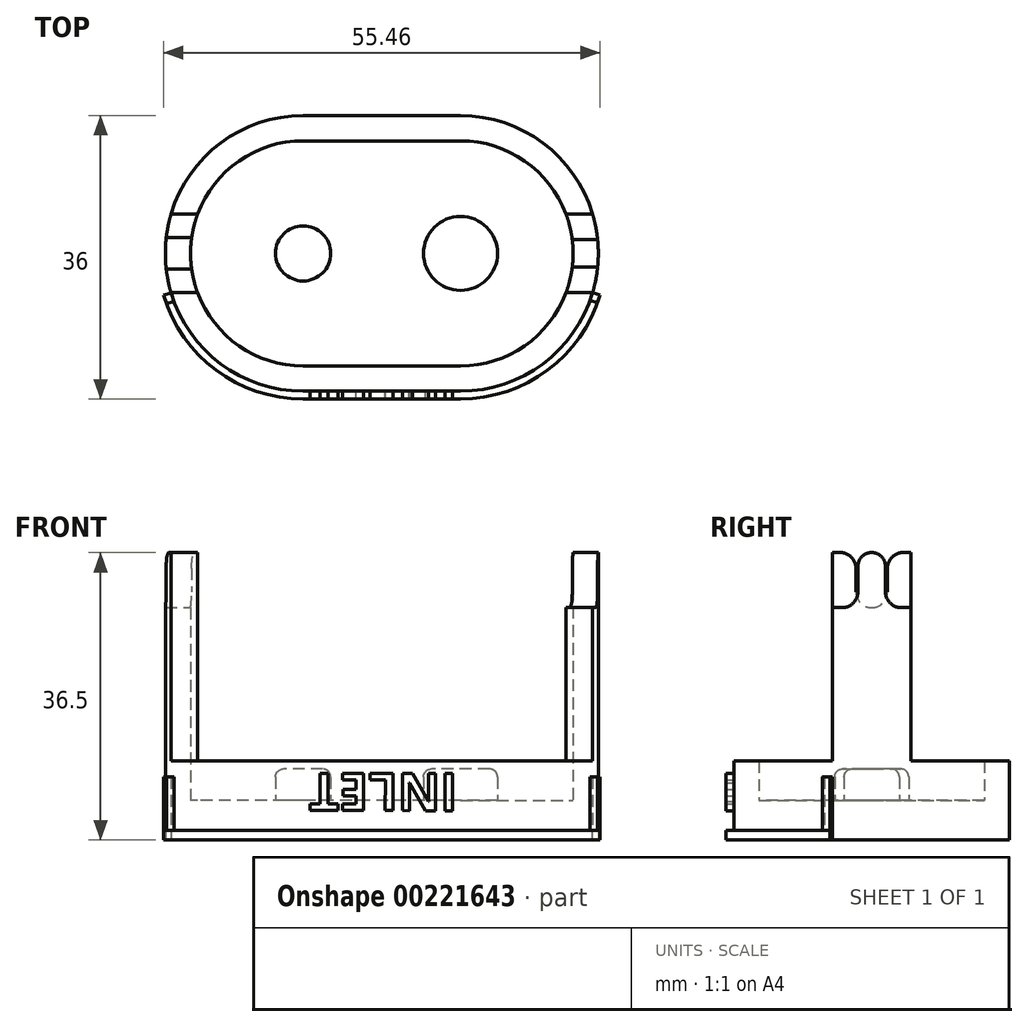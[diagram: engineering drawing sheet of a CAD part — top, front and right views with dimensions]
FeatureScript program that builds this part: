
annotation { "Feature Type Name" : "Feature", "Feature Type Description" : "" }
export const myFeature = defineFeature(function(context is Context, id is Id, definition is map)
    precondition{}
    {
        {
            var Q0;
            Q0=qCreatedBy(makeId("Top.planeOp"),FACE);
            var sketch = newSketch(context, id + "F0", { "sketchPlane" : qUnion([Q0])});
            skArc(sketch, "E0", {"start": v(0, -17.5) * mm, "mid": v(17.5, 0) * mm, "end": v(0, 17.5) * mm});
            skArc(sketch, "E1", {"start": v(-20, 17.5) * mm, "mid": v(-37.5, 0) * mm, "end": v(-20, -17.5) * mm});
            skLineSegment(sketch, "E2", {"start": v(-20, 17.5) * mm, "end": v(0, 17.5) * mm});
            skLineSegment(sketch, "E3", {"start": v(-20, -17.5) * mm, "end": v(0, -17.5) * mm});
            skSolve(sketch);
        }
        {
            var Q0;
            Q0=makeQuery(id+"F0.imprint","IMPRINT",FACE,{"disambiguationData":[TD([[makeQuery(id+"F0.imprint","IMPRINT",EDGE,{"derivedFrom":sQuery(id+"F0.wireOp",EDGE,"E0")}),1.0]])]});
            extrude(context, id + "F1", {"entities" : qUnion([Q0]), "depth" : 5 * mm});
        }
        {
            var Q0;
            Q0=qCreatedBy(makeId("Top.planeOp"),FACE);
            var sketch = newSketch(context, id + "F2", { "sketchPlane" : qUnion([Q0])});
            skArc(sketch, "E4", {"start": v(0, -17.5) * mm, "mid": v(17.5, 0) * mm, "end": v(0, 17.5) * mm});
            skArc(sketch, "E5", {"start": v(-20, 17.5) * mm, "mid": v(-37.5, 0) * mm, "end": v(-20, -17.5) * mm});
            skLineSegment(sketch, "E6", {"start": v(-20, 17.5) * mm, "end": v(0, 17.5) * mm});
            skLineSegment(sketch, "E7", {"start": v(-20, -17.5) * mm, "end": v(0, -17.5) * mm});
            skLineSegment(sketch, "E8.0", {"start": v(-20, 14.3) * mm, "end": v(0, 14.3) * mm});
            skArc(sketch, "E8.1", {"start": v(-20, 14.3) * mm, "mid": v(-34.3, 0) * mm, "end": v(-20, -14.3) * mm});
            skLineSegment(sketch, "E8.2", {"start": v(-20, -14.3) * mm, "end": v(0, -14.3) * mm});
            skArc(sketch, "E8.3", {"start": v(0, -14.3) * mm, "mid": v(14.3, 0) * mm, "end": v(0, 14.3) * mm});
            skSolve(sketch);
        }
        {
            var Q0;
            Q0 = qSketchRegion(id + "F2", true);
            extrude(context, id + "F3", {"entities" : qUnion([Q0]), "operationType" : NewBodyOperationType.ADD, "depth" : 10 * mm});
        }
        {
            var Q0;
            Q0=qCreatedBy(makeId("Top.planeOp"),FACE);
            var sketch = newSketch(context, id + "F4", { "sketchPlane" : qUnion([Q0])});
            skArc(sketch, "E9", {"start": v(16.77, -5) * mm, "mid": v(17.5, 0) * mm, "end": v(16.77, 5) * mm});
            skArc(sketch, "E10", {"start": v(-36.77, 5) * mm, "mid": v(-37.5, 0) * mm, "end": v(-36.77, -5) * mm});
            skArc(sketch, "E11.1", {"start": v(-33.4, 5) * mm, "mid": v(-34.3, 0) * mm, "end": v(-33.4, -5) * mm});
            skLineSegment(sketch, "E12.bottom", {"start": v(16.77, 5) * mm, "end": v(13.4, 5) * mm});
            skLineSegment(sketch, "E12.top", {"start": v(16.77, -5) * mm, "end": v(13.4, -5) * mm});
            skPoint(sketch, "E13.middle", {"position": v(-10, 0) * mm});
            skLineSegment(sketch, "E14.trimOffspring", {"start": v(-33.4, 5) * mm, "end": v(-36.77, 5) * mm});
            skLineSegment(sketch, "E15.trimOffspring", {"start": v(-33.4, -5) * mm, "end": v(-36.77, -5) * mm});
            skPoint(sketch, "E16", {"position": v(-34.3, 0) * mm});
            skArc(sketch, "E17", {"start": v(13.4, -5) * mm, "mid": v(14.3, 0) * mm, "end": v(13.4, 5) * mm});
            skSolve(sketch);
        }
        {
            var Q0;
            Q0=makeQuery(id+"F4.imprint","IMPRINT",FACE,{"disambiguationData":[TD([[makeQuery(id+"F4.imprint","IMPRINT",EDGE,{"derivedFrom":sQuery(id+"F4.wireOp",EDGE,"E9")}),1.0]])]});
            var Q1;
            Q1=makeQuery(id+"F4.imprint","IMPRINT",FACE,{"disambiguationData":[TD([[makeQuery(id+"F4.imprint","IMPRINT",EDGE,{"derivedFrom":sQuery(id+"F4.wireOp",EDGE,"E10")}),1.0]])]});
            extrude(context, id + "F5", {"entities" : qUnion([Q0, Q1]), "operationType" : NewBodyOperationType.ADD, "depth" : 36.5 * mm});
        }
        {
            var Q0;
            Q0=qCreatedBy(makeId("Right.planeOp"),FACE);
            var sketch = newSketch(context, id + "F6", { "sketchPlane" : qUnion([Q0])});
            skLineSegment(sketch, "E18.bottom", {"start": v(-2, 29.5) * mm, "end": v(2, 29.5) * mm});
            skLineSegment(sketch, "E18.top", {"start": v(-2, 39.5) * mm, "end": v(2, 39.5) * mm});
            skLineSegment(sketch, "E18.left", {"start": v(-2, 29.5) * mm, "end": v(-2, 39.5) * mm});
            skLineSegment(sketch, "E18.right", {"start": v(2, 29.5) * mm, "end": v(2, 39.5) * mm});
            skPoint(sketch, "E18.middle", {"position": v(0, 34.5) * mm});
            skSolve(sketch);
        }
        {
            var Q0;
            Q0=makeQuery(id+"F6.imprint","IMPRINT",FACE,{"disambiguationData":[TD([[makeQuery(id+"F6.imprint","IMPRINT",EDGE,{"derivedFrom":sQuery(id+"F6.wireOp",EDGE,"E18.bottom")}),1.0]])]});
            extrude(context, id + "F7", {"entities" : qUnion([Q0]), "operationType" : NewBodyOperationType.REMOVE, "oppositeDirection" : true, "depth" : 43.6 * mm});
        }
        {
            var Q0;
            Q0=qCreatedBy(makeId("Right.planeOp"),FACE);
            var sketch = newSketch(context, id + "F8", { "sketchPlane" : qUnion([Q0])});
            skLineSegment(sketch, "E19.bottom", {"start": v(-1.75, 29.5) * mm, "end": v(-5.7, 29.5) * mm});
            skLineSegment(sketch, "E19.top", {"start": v(-1.75, 39.5) * mm, "end": v(-5.7, 39.5) * mm});
            skLineSegment(sketch, "E19.left", {"start": v(-1.75, 29.5) * mm, "end": v(-1.75, 39.5) * mm});
            skLineSegment(sketch, "E19.right", {"start": v(-5.7, 29.5) * mm, "end": v(-5.7, 39.5) * mm});
            skPoint(sketch, "E19.middle", {"position": v(-3.72, 34.5) * mm});
            skLineSegment(sketch, "E20.bottom", {"start": v(5.7, 29.5) * mm, "end": v(1.75, 29.5) * mm});
            skLineSegment(sketch, "E20.top", {"start": v(5.7, 39.5) * mm, "end": v(1.75, 39.5) * mm});
            skLineSegment(sketch, "E20.left", {"start": v(5.7, 29.5) * mm, "end": v(5.7, 39.5) * mm});
            skLineSegment(sketch, "E20.right", {"start": v(1.75, 29.5) * mm, "end": v(1.75, 39.5) * mm});
            skPoint(sketch, "E20.middle", {"position": v(3.72, 34.5) * mm});
            skLineSegment(sketch, "E21", {"start": v(-3.72, 34.5) * mm, "end": v(3.72, 34.5) * mm});
            skPoint(sketch, "E22", {"position": v(0, 34.5) * mm});
            skSolve(sketch);
        }
        {
            var Q0;
            {var subQ1=sQuery(id+"F8.wireOp",EDGE,"E20.bottom");Q0=makeQuery(id+"F8.imprint","IMPRINT",FACE,{"disambiguationData":[TD([[makeQuery(id+"F8.imprint","IMPRINT",EDGE,{"derivedFrom":subQ1}),-1.0]])]});}
            var Q1;
            {var subQ3=sQuery(id+"F8.wireOp",EDGE,"E19.bottom");Q1=makeQuery(id+"F8.imprint","IMPRINT",FACE,{"disambiguationData":[TD([[makeQuery(id+"F8.imprint","IMPRINT",EDGE,{"derivedFrom":subQ3}),-1.0]])]});}
            extrude(context, id + "F9", {"entities" : qUnion([Q0, Q1]), "operationType" : NewBodyOperationType.REMOVE, "depth" : 25 * mm});
        }
        {
            var Q0;
            Q0=makeQuery(id+"F7.boolean.opBoolean","COPY",EDGE,{"derivedFrom":makeQuery(id+"F7.opExtrude","SWEPT_EDGE",EDGE,{"disambiguationData":[OSD([sQuery(id+"F6.wireOp",EDGE,"E18.bottom"),sQuery(id+"F6.wireOp",EDGE,"E18.left")])]})});
            var Q1;
            Q1=makeQuery(id+"F7.boolean.opBoolean","COPY",EDGE,{"derivedFrom":makeQuery(id+"F7.opExtrude","SWEPT_EDGE",EDGE,{"disambiguationData":[OSD([sQuery(id+"F6.wireOp",EDGE,"E18.bottom"),sQuery(id+"F6.wireOp",EDGE,"E18.right")])]})});
            fillet(context, id + "F10", {"entities" : qUnion([Q0, Q1]), "radius" : 2 * mm, "tangentPropagation" : true, "allowEdgeOverflow" : false});
        }
        {
            var Q0;
            Q0=makeQuery(id+"F9.boolean.opBoolean","INTERSECT",EDGE,{"derivedFrom":[makeQuery(id+"F5.opExtrude","CAP_FACE",FACE,{"disambiguationData":[OSD([sQuery(id+"F4.wireOp",EDGE,"E9"),sQuery(id+"F4.wireOp",EDGE,"E12.bottom"),sQuery(id+"F4.wireOp",EDGE,"E12.top"),sQuery(id+"F4.wireOp",EDGE,"E17")])],"isStart":false}),makeQuery(id+"F9.opExtrude","SWEPT_FACE",FACE,{"disambiguationData":[OSD([sQuery(id+"F8.wireOp",EDGE,"E19.left")])]})]});
            var Q1;
            Q1=makeQuery(id+"F9.boolean.opBoolean","INTERSECT",EDGE,{"derivedFrom":[makeQuery(id+"F5.opExtrude","CAP_FACE",FACE,{"disambiguationData":[OSD([sQuery(id+"F4.wireOp",EDGE,"E9"),sQuery(id+"F4.wireOp",EDGE,"E12.bottom"),sQuery(id+"F4.wireOp",EDGE,"E12.top"),sQuery(id+"F4.wireOp",EDGE,"E17")])],"isStart":false}),makeQuery(id+"F9.opExtrude","SWEPT_FACE",FACE,{"disambiguationData":[OSD([sQuery(id+"F8.wireOp",EDGE,"E20.right")])]})]});
            fillet(context, id + "F11", {"entities" : qUnion([Q0, Q1]), "radius" : 1.75 * mm, "tangentPropagation" : true, "allowEdgeOverflow" : false});
        }
        {
            var Q0;
            Q0=makeQuery(id+"F9.boolean.opBoolean","COPY",EDGE,{"derivedFrom":makeQuery(id+"F9.opExtrude","SWEPT_EDGE",EDGE,{"disambiguationData":[OSD([sQuery(id+"F8.wireOp",EDGE,"E19.bottom"),sQuery(id+"F8.wireOp",EDGE,"E19.left")])]})});
            var Q1;
            Q1=makeQuery(id+"F9.boolean.opBoolean","COPY",EDGE,{"derivedFrom":makeQuery(id+"F9.opExtrude","SWEPT_EDGE",EDGE,{"disambiguationData":[OSD([sQuery(id+"F8.wireOp",EDGE,"E20.bottom"),sQuery(id+"F8.wireOp",EDGE,"E20.right")])]})});
            var Q2;
            Q2=makeQuery(id+"F7.boolean.opBoolean","INTERSECT",EDGE,{"derivedFrom":[makeQuery(id+"F5.opExtrude","CAP_FACE",FACE,{"disambiguationData":[OSD([sQuery(id+"F4.wireOp",EDGE,"E10"),sQuery(id+"F4.wireOp",EDGE,"E11.1"),sQuery(id+"F4.wireOp",EDGE,"E14.trimOffspring"),sQuery(id+"F4.wireOp",EDGE,"E15.trimOffspring")])],"isStart":false}),makeQuery(id+"F7.opExtrude","SWEPT_FACE",FACE,{"disambiguationData":[OSD([sQuery(id+"F6.wireOp",EDGE,"E18.left")])]})]});
            var Q3;
            Q3=makeQuery(id+"F7.boolean.opBoolean","INTERSECT",EDGE,{"derivedFrom":[makeQuery(id+"F5.opExtrude","CAP_FACE",FACE,{"disambiguationData":[OSD([sQuery(id+"F4.wireOp",EDGE,"E10"),sQuery(id+"F4.wireOp",EDGE,"E11.1"),sQuery(id+"F4.wireOp",EDGE,"E14.trimOffspring"),sQuery(id+"F4.wireOp",EDGE,"E15.trimOffspring")])],"isStart":false}),makeQuery(id+"F7.opExtrude","SWEPT_FACE",FACE,{"disambiguationData":[OSD([sQuery(id+"F6.wireOp",EDGE,"E18.right")])]})]});
            fillet(context, id + "F12", {"entities" : qUnion([Q0, Q1, Q2, Q3]), "radius" : 2 * mm, "tangentPropagation" : true, "allowEdgeOverflow" : false});
        }
        {
            var Q0;
            Q0=qCreatedBy(makeId("Top.planeOp"),FACE);
            var sketch = newSketch(context, id + "F13", { "sketchPlane" : qUnion([Q0])});
            skCircle(sketch, "E23", {"center": v(0, 0) * mm, "radius": 4.7 * mm});
            skCircle(sketch, "E24", {"center": v(-20, 0) * mm, "radius": 3.5 * mm});
            skSolve(sketch);
        }
        {
            var Q0;
            Q0 = qSketchRegion(id + "F13", true);
            extrude(context, id + "F14", {"entities" : qUnion([Q0]), "operationType" : NewBodyOperationType.ADD, "depth" : 9 * mm});
        }
        {
            var Q0;
            Q0=makeQuery(id+"F14.opExtrude","CAP_EDGE",EDGE,{"disambiguationData":[OSD([sQuery(id+"F13.wireOp",EDGE,"E23")])],"isStart":false});
            var Q1;
            Q1=makeQuery(id+"F14.opExtrude","CAP_EDGE",EDGE,{"disambiguationData":[OSD([sQuery(id+"F13.wireOp",EDGE,"E24")])],"isStart":false});
            fillet(context, id + "F15", {"entities" : qUnion([Q0, Q1]), "radius" : 1 * mm, "tangentPropagation" : true, "allowEdgeOverflow" : false});
        }
        {
            var Q0;
            Q0=makeQuery(id+"F3.boolean.opBoolean","MERGE",FACE,{"derivedFrom":[makeQuery(id+"F1.opExtrude","SWEPT_FACE",FACE,{"disambiguationData":[OSD([sQuery(id+"F0.wireOp",EDGE,"E3")])]}),makeQuery(id+"F3.opExtrude","SWEPT_FACE",FACE,{"disambiguationData":[OSD([sQuery(id+"F2.wireOp",EDGE,"E7")])]})]});
            var sketch = newSketch(context, id + "F16", { "sketchPlane" : qUnion([Q0])});
            skText(sketch, "E25", { "text": "INLET", "fontName": "OpenSans-Bold.ttf"});
            skLineSegment(sketch, "E26", {"start": v(0, 0) * mm, "end": v(89.93, 0) * mm});
            const initialGuessF16  = {"E25": [-0.0004, 0.00842, -1, 0.00167, 0.00476]};
            skSetInitialGuess(sketch, initialGuessF16);
            skSolve(sketch);
        }
        {
            var Q0;
            Q0 = qSketchRegion(id + "F16", true);
            extrude(context, id + "F17", {"entities" : qUnion([Q0]), "operationType" : NewBodyOperationType.ADD, "depth" : 1 * mm});
        }
        {
            var Q0;
            Q0=qCreatedBy(makeId("Top.planeOp"),FACE);
            var sketch = newSketch(context, id + "F18", { "sketchPlane" : qUnion([Q0])});
            skArc(sketch, "E27.0", {"start": v(0, -18.5) * mm, "mid": v(11.06, -14.83) * mm, "end": v(17.73, -5.29) * mm});
            skLineSegment(sketch, "E27.1", {"start": v(-20, -18.5) * mm, "end": v(0, -18.5) * mm});
            skArc(sketch, "E27.2", {"start": v(-37.73, -5.29) * mm, "mid": v(-31.06, -14.83) * mm, "end": v(-20, -18.5) * mm});
            skArc(sketch, "E28.0", {"start": v(0, -17.5) * mm, "mid": v(10.46, -14.03) * mm, "end": v(16.77, -5) * mm});
            skLineSegment(sketch, "E28.1", {"start": v(-20, -17.5) * mm, "end": v(0, -17.5) * mm});
            skArc(sketch, "E28.2", {"start": v(-36.77, -5) * mm, "mid": v(-30.46, -14.03) * mm, "end": v(-20, -17.5) * mm});
            skLineSegment(sketch, "E29", {"start": v(-36.77, -5) * mm, "end": v(-37.73, -5.29) * mm});
            skLineSegment(sketch, "E30", {"start": v(17.73, -5.29) * mm, "end": v(16.77, -5) * mm});
            skSolve(sketch);
        }
        {
            var Q0;
            Q0=makeQuery(id+"F18.imprint","IMPRINT",FACE,{"disambiguationData":[TD([[makeQuery(id+"F18.imprint","IMPRINT",EDGE,{"derivedFrom":sQuery(id+"F18.wireOp",EDGE,"E27.0")}),1.0]])]});
            extrude(context, id + "F19", {"entities" : qUnion([Q0]), "operationType" : NewBodyOperationType.ADD, "depth" : 1.2 * mm});
        }
        {
            var Q0;
            Q0=qCreatedBy(makeId("Top.planeOp"),FACE);
            var sketch = newSketch(context, id + "F20", { "sketchPlane" : qUnion([Q0])});
            skLineSegment(sketch, "E31", {"start": v(-37.73, -5.29) * mm, "end": v(-36.35, -4.89) * mm});
            skLineSegment(sketch, "E32", {"start": v(-36.35, -4.89) * mm, "end": v(-36.03, -5.99) * mm});
            skLineSegment(sketch, "E33", {"start": v(-36.03, -5.99) * mm, "end": v(-37.36, -6.37) * mm});
            skLineSegment(sketch, "E34", {"start": v(-37.36, -6.37) * mm, "end": v(-37.73, -5.29) * mm});
            skLineSegment(sketch, "E35", {"start": v(17.73, -5.29) * mm, "end": v(16.54, -4.93) * mm});
            skLineSegment(sketch, "E36", {"start": v(16.54, -4.93) * mm, "end": v(16.24, -5.92) * mm});
            skLineSegment(sketch, "E37", {"start": v(16.24, -5.92) * mm, "end": v(17.4, -6.26) * mm});
            skLineSegment(sketch, "E38", {"start": v(17.4, -6.26) * mm, "end": v(17.73, -5.29) * mm});
            skSolve(sketch);
        }
        {
            var Q0;
            Q0 = qSketchRegion(id + "F20", true);
            extrude(context, id + "F21", {"entities" : qUnion([Q0]), "operationType" : NewBodyOperationType.ADD, "depth" : 8 * mm});
        }
    });
